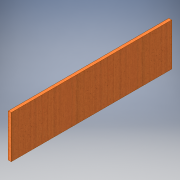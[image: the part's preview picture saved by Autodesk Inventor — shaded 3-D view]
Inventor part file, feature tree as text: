
AUTODESK INVENTOR PART (.ipt)
format: ipt  version: 2016 (Build 200138000, 138)  size: 102,400 bytes
history: native  units: in
note: dims shown in document units (in); Inventor stores cm internally (conversion verified against a paired STEP export)
features: extrude x1, sketch x1
ambient origin geometry x8: Origin, YZ Plane, XZ Plane, XY Plane, X Axis, Y Axis, Z Axis, Center Point
bodies: Solid1 (feature_tree)
feature tree (2):
  extrude  "Extrusion1"  Depth=6.5in
  sketch  "Sketch1"  dims[d0=24.5in d1=6.5in d2=0.4375in d3=0.0in]
